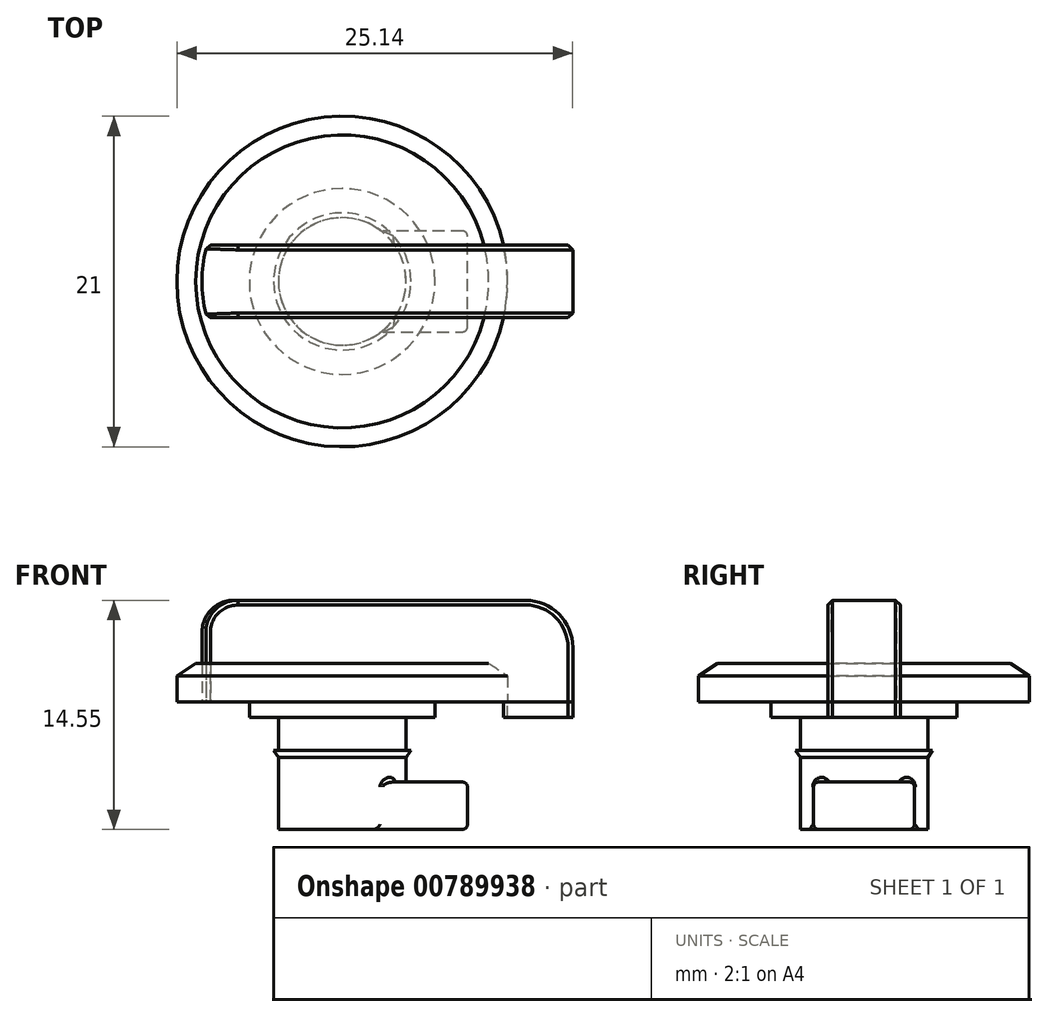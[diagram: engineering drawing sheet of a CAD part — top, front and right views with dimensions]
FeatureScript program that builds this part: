
annotation { "Feature Type Name" : "Feature", "Feature Type Description" : "" }
export const myFeature = defineFeature(function(context is Context, id is Id, definition is map)
    precondition{}
    {
        {
            var Q0;
            Q0=qCreatedBy(makeId("Top.planeOp"),FACE);
            var sketch = newSketch(context, id + "F0", { "sketchPlane" : qUnion([Q0])});
            skCircle(sketch, "E0", {"center": v(0, 0) * mm, "radius": 10.5 * mm});
            skCircle(sketch, "E1", {"center": v(0, 0) * mm, "radius": 8.9 * mm});
            skLineSegment(sketch, "E2", {"start": v(-8.6, 2.3) * mm, "end": v(14.64, 2.3) * mm});
            skLineSegment(sketch, "E3", {"start": v(-8.6, -2.3) * mm, "end": v(14.64, -2.3) * mm});
            skLineSegment(sketch, "E4", {"start": v(10.24, 2.3) * mm, "end": v(10.24, 9.1) * mm, "construction": true});
            skLineSegment(sketch, "E5", {"start": v(14.64, 2.3) * mm, "end": v(14.64, -2.3) * mm});
            skPoint(sketch, "E6.orphan", {"position": v(14.64, -4.07) * mm});
            skPoint(sketch, "E7.orphan", {"position": v(14.64, -2.3) * mm});
            skSolve(sketch);
        }
        {
            var Q0;
            {var subQ0=sQuery(id+"F0.wireOp",EDGE,"E2");var subQ1=sQuery(id+"F0.wireOp",EDGE,"E0");var subQ2=makeQuery(id+"F0.imprint","INTERSECT",VERTEX,{"derivedFrom":[subQ1,subQ0]});Q0=makeQuery(id+"F0.imprint","IMPRINT",FACE,{"disambiguationData":[TD([[makeQuery(id+"F0.imprint","IMPRINT",EDGE,{"disambiguationData":[TD([[subQ2,1.0]])],"derivedFrom":subQ1}),1.0]])]});}
            var Q1;
            {var subQ4=sQuery(id+"F0.wireOp",EDGE,"E2");var subQ7=sQuery(id+"F0.wireOp",EDGE,"E0");var subQ8=makeQuery(id+"F0.imprint","INTERSECT",VERTEX,{"derivedFrom":[subQ7,subQ4]});Q1=makeQuery(id+"F0.imprint","IMPRINT",FACE,{"disambiguationData":[TD([[makeQuery(id+"F0.imprint","IMPRINT",EDGE,{"disambiguationData":[TD([[subQ8,-1.0]])],"derivedFrom":subQ7}),1.0]])]});}
            var Q2;
            {var subQ0=sQuery(id+"F0.wireOp",EDGE,"E2");var subQ1=sQuery(id+"F0.wireOp",EDGE,"E1");var subQ2=makeQuery(id+"F0.imprint","INTERSECT",VERTEX,{"disambiguationData":[OD(0.0)],"derivedFrom":[subQ1,subQ0]});Q2=makeQuery(id+"F0.imprint","IMPRINT",FACE,{"disambiguationData":[TD([[makeQuery(id+"F0.imprint","IMPRINT",EDGE,{"disambiguationData":[TD([[subQ2,1.0]])],"derivedFrom":subQ1}),1.0]])]});}
            var Q3;
            {var subQ0=sQuery(id+"F0.wireOp",EDGE,"E3");var subQ1=sQuery(id+"F0.wireOp",EDGE,"E1");var subQ2=makeQuery(id+"F0.imprint","INTERSECT",VERTEX,{"disambiguationData":[OD(0.0)],"derivedFrom":[subQ1,subQ0]});Q3=makeQuery(id+"F0.imprint","IMPRINT",FACE,{"disambiguationData":[TD([[makeQuery(id+"F0.imprint","IMPRINT",EDGE,{"disambiguationData":[TD([[subQ2,-1.0]])],"derivedFrom":subQ1}),1.0]])]});}
            var Q4;
            {var subQ0=sQuery(id+"F0.wireOp",EDGE,"E2");var subQ1=sQuery(id+"F0.wireOp",EDGE,"E1");var subQ2=makeQuery(id+"F0.imprint","INTERSECT",VERTEX,{"disambiguationData":[OD(0.0)],"derivedFrom":[subQ1,subQ0]});Q4=makeQuery(id+"F0.imprint","IMPRINT",FACE,{"disambiguationData":[TD([[makeQuery(id+"F0.imprint","IMPRINT",EDGE,{"disambiguationData":[TD([[subQ2,-1.0]])],"derivedFrom":subQ1}),1.0]])]});}
            extrude(context, id + "F1", {"entities" : qUnion([Q0, Q1, Q2, Q3, Q4]), "depth" : 2.45 * mm, "offsetDistance" : 25 * mm});
        }
        {
            var Q0;
            {var subQ5=sQuery(id+"F0.wireOp",EDGE,"E5");Q0=makeQuery(id+"F0.imprint","IMPRINT",FACE,{"disambiguationData":[TD([[makeQuery(id+"F0.imprint","IMPRINT",EDGE,{"derivedFrom":subQ5}),-1.0]])]});}
            extrude(context, id + "F2", {"entities" : qUnion([Q0]), "depth" : -1 * mm, "offsetDistance" : 25 * mm});
        }
        {
            var Q0;
            {var subQ5=sQuery(id+"F0.wireOp",EDGE,"E5");Q0=makeQuery(id+"F0.imprint","IMPRINT",FACE,{"disambiguationData":[TD([[makeQuery(id+"F0.imprint","IMPRINT",EDGE,{"derivedFrom":subQ5}),-1.0]])]});}
            var Q1;
            {var subQ0=sQuery(id+"F0.wireOp",EDGE,"E2");var subQ1=sQuery(id+"F0.wireOp",EDGE,"E0");var subQ2=makeQuery(id+"F0.imprint","INTERSECT",VERTEX,{"derivedFrom":[subQ1,subQ0]});Q1=makeQuery(id+"F0.imprint","IMPRINT",FACE,{"disambiguationData":[TD([[makeQuery(id+"F0.imprint","IMPRINT",EDGE,{"disambiguationData":[TD([[subQ2,1.0]])],"derivedFrom":subQ1}),1.0]])]});}
            var Q2;
            {var subQ0=sQuery(id+"F0.wireOp",EDGE,"E2");var subQ1=sQuery(id+"F0.wireOp",EDGE,"E1");var subQ2=makeQuery(id+"F0.imprint","INTERSECT",VERTEX,{"disambiguationData":[OD(0.0)],"derivedFrom":[subQ1,subQ0]});Q2=makeQuery(id+"F0.imprint","IMPRINT",FACE,{"disambiguationData":[TD([[makeQuery(id+"F0.imprint","IMPRINT",EDGE,{"disambiguationData":[TD([[subQ2,-1.0]])],"derivedFrom":subQ1}),1.0]])]});}
            extrude(context, id + "F3", {"entities" : qUnion([Q0, Q1, Q2]), "depth" : 6.45 * mm, "offsetDistance" : 25 * mm});
        }
        {
            var Q0;
            Q0=makeQuery(id+"F1.opExtrude","CAP_EDGE",EDGE,{"disambiguationData":[OSD([sQuery(id+"F0.wireOp",EDGE,"E0")])],"isStart":false});
            chamfer(context, id + "F4", {"entities" : qUnion([Q0]), "chamferType" : ChamferType.TWO_OFFSETS, "width1" : 1.2 * mm, "oppositeDirection" : false, "width2" : 0.8 * mm, "tangentPropagation" : true});
        }
        {
            var Q0;
            Q0=makeQuery(id+"F3.opExtrude","CAP_EDGE",EDGE,{"disambiguationData":[OSD([sQuery(id+"F0.wireOp",EDGE,"E5")])],"isStart":false});
            fillet(context, id + "F5", {"entities" : qUnion([Q0]), "radius" : 3 * mm, "tangentPropagation" : true, "allowEdgeOverflow" : false});
        }
        {
            var Q0;
            Q0=makeQuery(id+"F3.opExtrude","CAP_EDGE",EDGE,{"disambiguationData":[OSD([sQuery(id+"F0.wireOp",EDGE,"E1")])],"isStart":false});
            fillet(context, id + "F6", {"entities" : qUnion([Q0]), "radius" : 2 * mm, "tangentPropagation" : true, "allowEdgeOverflow" : false});
        }
        {
            var Q0;
            Q0=makeQuery(id+"F3.opExtrude","CAP_EDGE",EDGE,{"disambiguationData":[OSD([sQuery(id+"F0.wireOp",EDGE,"E2")])],"isStart":false});
            var Q1;
            Q1=makeQuery(id+"F3.opExtrude","CAP_EDGE",EDGE,{"disambiguationData":[OSD([sQuery(id+"F0.wireOp",EDGE,"E3")])],"isStart":false});
            var Q2;
            Q2=makeQuery(id+"F5.opFillet","BLEND_EDGE",EDGE,{"blendedFrom":[makeQuery(id+"F3.opExtrude","CAP_EDGE",EDGE,{"disambiguationData":[OSD([sQuery(id+"F0.wireOp",EDGE,"E5")])],"isStart":false}),makeQuery(id+"F3.opExtrude","SWEPT_FACE",FACE,{"disambiguationData":[OSD([sQuery(id+"F0.wireOp",EDGE,"E2")])]})],"blendedInto":[makeQuery(id+"F3.opExtrude","SWEPT_FACE",FACE,{"disambiguationData":[OSD([sQuery(id+"F0.wireOp",EDGE,"E2")])]})]});
            var Q3;
            Q3=makeQuery(id+"F5.opFillet","BLEND_EDGE",EDGE,{"blendedFrom":[makeQuery(id+"F3.opExtrude","CAP_EDGE",EDGE,{"disambiguationData":[OSD([sQuery(id+"F0.wireOp",EDGE,"E5")])],"isStart":false}),makeQuery(id+"F3.opExtrude","SWEPT_FACE",FACE,{"disambiguationData":[OSD([sQuery(id+"F0.wireOp",EDGE,"E3")])]})],"blendedInto":[makeQuery(id+"F3.opExtrude","SWEPT_FACE",FACE,{"disambiguationData":[OSD([sQuery(id+"F0.wireOp",EDGE,"E3")])]})]});
            var Q4;
            Q4=makeQuery(id+"F3.opExtrude","SWEPT_EDGE",EDGE,{"disambiguationData":[OSD([sQuery(id+"F0.wireOp",EDGE,"E3"),sQuery(id+"F0.wireOp",EDGE,"E5")])]});
            var Q5;
            Q5=makeQuery(id+"F3.opExtrude","SWEPT_EDGE",EDGE,{"disambiguationData":[OSD([sQuery(id+"F0.wireOp",EDGE,"E2"),sQuery(id+"F0.wireOp",EDGE,"E5")])]});
            var Q6;
            Q6=makeQuery(id+"F6.opFillet","BLEND_EDGE",EDGE,{"blendedFrom":[makeQuery(id+"F3.opExtrude","CAP_EDGE",EDGE,{"disambiguationData":[OSD([sQuery(id+"F0.wireOp",EDGE,"E1")])],"isStart":false}),makeQuery(id+"F3.opExtrude","SWEPT_FACE",FACE,{"disambiguationData":[OSD([sQuery(id+"F0.wireOp",EDGE,"E2")])]})],"blendedInto":[makeQuery(id+"F3.opExtrude","SWEPT_FACE",FACE,{"disambiguationData":[OSD([sQuery(id+"F0.wireOp",EDGE,"E2")])]})]});
            var Q7;
            Q7=makeQuery(id+"F3.opExtrude","SWEPT_EDGE",EDGE,{"disambiguationData":[OSD([sQuery(id+"F0.wireOp",EDGE,"E1"),sQuery(id+"F0.wireOp",EDGE,"E2")])]});
            var Q8;
            Q8=makeQuery(id+"F3.opExtrude","SWEPT_EDGE",EDGE,{"disambiguationData":[OSD([sQuery(id+"F0.wireOp",EDGE,"E1"),sQuery(id+"F0.wireOp",EDGE,"E3")])]});
            var Q9;
            Q9=makeQuery(id+"F2.opExtrude","SWEPT_EDGE",EDGE,{"disambiguationData":[OSD([sQuery(id+"F0.wireOp",EDGE,"E2"),sQuery(id+"F0.wireOp",EDGE,"E5")])]});
            var Q10;
            Q10=makeQuery(id+"F2.opExtrude","SWEPT_EDGE",EDGE,{"disambiguationData":[OSD([sQuery(id+"F0.wireOp",EDGE,"E3"),sQuery(id+"F0.wireOp",EDGE,"E5")])]});
            chamfer(context, id + "F7", {"entities" : qUnion([Q0, Q1, Q2, Q3, Q4, Q5, Q6, Q7, Q8, Q9, Q10]), "width" : 0.3 * mm, "tangentPropagation" : true});
        }
        {
            var Q0;
            Q0=qCreatedBy(makeId("Top.planeOp"),FACE);
            var sketch = newSketch(context, id + "F8", { "sketchPlane" : qUnion([Q0])});
            skCircle(sketch, "E8", {"center": v(0, 0) * mm, "radius": 5.9 * mm});
            skSolve(sketch);
        }
        {
            var Q0;
            Q0=qSketchRegion(id+"F8",true);
            extrude(context, id + "F9", {"entities" : qUnion([Q0]), "depth" : -1 * mm, "offsetDistance" : 25 * mm});
        }
        {
            var Q0;
            Q0=makeQuery(id+"F9.opExtrude","CAP_FACE",FACE,{"disambiguationData":[OSD([sQuery(id+"F8.wireOp",EDGE,"E8")])],"isStart":false});
            var sketch = newSketch(context, id + "F10", { "sketchPlane" : qUnion([Q0])});
            skCircle(sketch, "E9", {"center": v(0, 0) * mm, "radius": 4.05 * mm});
            skSolve(sketch);
        }
        {
            var Q0;
            Q0=makeQuery(id+"F10.imprint","IMPRINT",FACE,{"disambiguationData":[TD([[makeQuery(id+"F10.imprint","IMPRINT",EDGE,{"derivedFrom":sQuery(id+"F10.wireOp",EDGE,"E9")}),1.0]])]});
            extrude(context, id + "F11", {"entities" : qUnion([Q0]), "operationType" : NewBodyOperationType.ADD, "depth" : 7.1 * mm, "offsetDistance" : 25 * mm});
        }
        {
            var Q0;
            Q0=makeQuery(id+"F11.opExtrude","CAP_FACE",FACE,{"disambiguationData":[OSD([sQuery(id+"F10.wireOp",EDGE,"E9")])],"isStart":false});
            var sketch = newSketch(context, id + "F12", { "sketchPlane" : qUnion([Q0])});
            skLineSegment(sketch, "E10", {"start": v(0, 3.2) * mm, "end": v(7.95, 3.2) * mm});
            skLineSegment(sketch, "E11", {"start": v(7.95, 3.2) * mm, "end": v(7.95, -3.2) * mm});
            skLineSegment(sketch, "E12", {"start": v(7.95, -3.2) * mm, "end": v(0, -3.2) * mm});
            skSolve(sketch);
        }
        {
            var Q0;
            {var subQ0=sQuery(id+"F12.wireOp",EDGE,"E11");Q0=makeQuery(id+"F12.imprint","IMPRINT",FACE,{"disambiguationData":[TD([[makeQuery(id+"F12.imprint","IMPRINT",EDGE,{"derivedFrom":subQ0}),-1.0]])]});}
            extrude(context, id + "F13", {"entities" : qUnion([Q0]), "operationType" : NewBodyOperationType.ADD, "depth" : -3 * mm, "offsetDistance" : 25 * mm});
        }
        {
            var Q0;
            Q0=makeQuery(id+"F13.opExtrude","SWEPT_FACE",FACE,{"disambiguationData":[OSD([sQuery(id+"F12.wireOp",EDGE,"E11")])]});
            var Q1;
            Q1=makeQuery(id+"F13.opExtrude","SWEPT_FACE",FACE,{"disambiguationData":[OSD([sQuery(id+"F12.wireOp",EDGE,"E12")])]});
            var Q2;
            Q2=makeQuery(id+"F13.opExtrude","SWEPT_FACE",FACE,{"disambiguationData":[OSD([sQuery(id+"F12.wireOp",EDGE,"E10")])]});
            fillet(context, id + "F14", {"entities" : qUnion([Q0, Q1, Q2]), "radius" : 0.3 * mm, "tangentPropagation" : true, "allowEdgeOverflow" : false});
        }
        {
            var Q0;
            {var subQ0=sQuery(id+"F10.wireOp",EDGE,"E9");Q0=makeQuery(id+"F13.boolean.opBoolean","MERGE",FACE,{"derivedFrom":[makeQuery(id+"F11.opExtrude","CAP_FACE",FACE,{"disambiguationData":[OSD([subQ0])],"isStart":false}),makeQuery(id+"F13.opExtrude","CAP_FACE",FACE,{"disambiguationData":[OSD([subQ0,sQuery(id+"F12.wireOp",EDGE,"E10"),sQuery(id+"F12.wireOp",EDGE,"E11"),sQuery(id+"F12.wireOp",EDGE,"E12")])],"isStart":true})]});}
            var sketch = newSketch(context, id + "F15", { "sketchPlane" : qUnion([Q0])});
            skCircle(sketch, "E13", {"center": v(0, 0) * mm, "radius": 4.5 * mm});
            skCircle(sketch, "E14", {"center": v(0, 0) * mm, "radius": 4.05 * mm});
            skSolve(sketch);
        }
        {
            var Q0;
            Q0=qSketchRegion(id+"F15",true);
            extrude(context, id + "F16", {"entities" : qUnion([Q0]), "operationType" : NewBodyOperationType.ADD, "depth" : -5 * mm, "offsetDistance" : 25 * mm, "hasSecondDirection" : true, "secondDirectionOppositeDirection" : true, "secondDirectionDepth" : 4.2 * mm});
        }
        {
            var Q0;
            Q0=makeQuery(id+"F16.opExtrude","CAP_EDGE",EDGE,{"disambiguationData":[OSD([sQuery(id+"F15.wireOp",EDGE,"E13")])],"isStart":true});
            chamfer(context, id + "F17", {"entities" : qUnion([Q0]), "chamferType" : ChamferType.TWO_OFFSETS, "width1" : .7 * mm, "oppositeDirection" : false, "width2" : 1 * mm, "tangentPropagation" : true});
        }
    });
